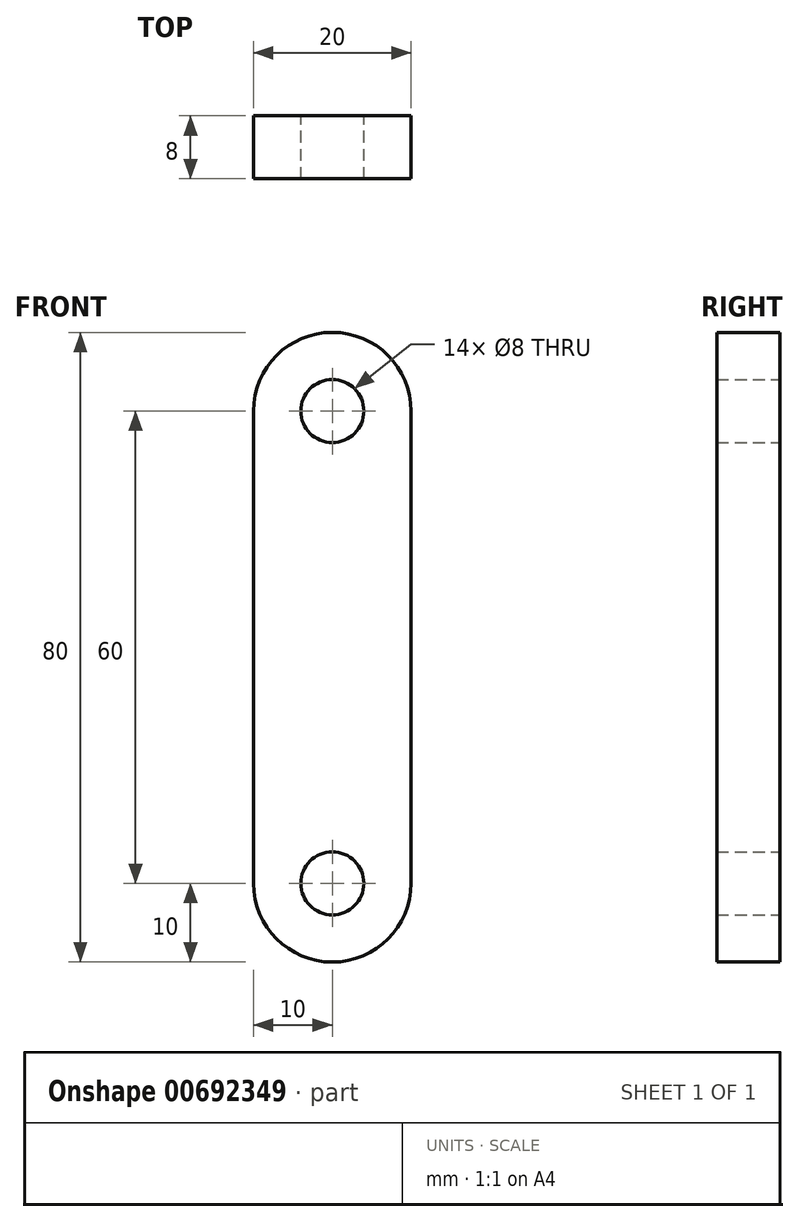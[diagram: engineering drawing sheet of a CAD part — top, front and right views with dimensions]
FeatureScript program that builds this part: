
annotation { "Feature Type Name" : "Feature", "Feature Type Description" : "" }
export const myFeature = defineFeature(function(context is Context, id is Id, definition is map)
    precondition{}
    {
        {
            var Q0;
            Q0=qCreatedBy(makeId("Front.planeOp"),FACE);
            var sketch = newSketch(context, id + "F0", { "sketchPlane" : qUnion([Q0])});
            skArc(sketch, "E0", {"start": v(-10, 0) * mm, "mid": v(0, -10) * mm, "end": v(10, 0) * mm});
            skCircle(sketch, "E1", {"center": v(0, 0) * mm, "radius": 4 * mm});
            skLineSegment(sketch, "E2", {"start": v(-10, 0) * mm, "end": v(-10, 60) * mm});
            skLineSegment(sketch, "E3", {"start": v(10, 60) * mm, "end": v(10, 0) * mm});
            skCircle(sketch, "E4", {"center": v(0, 60) * mm, "radius": 4 * mm});
            skArc(sketch, "E5", {"start": v(10, 60) * mm, "mid": v(0, 70) * mm, "end": v(-10, 60) * mm});
            skSolve(sketch);
        }
        {
            var Q0;
            Q0 = qSketchRegion(id + "F0", true);
            extrude(context, id + "F1", {"entities" : qUnion([Q0]), "depth" : 8 * mm, "offsetDistance" : 25 * mm});
        }
    });
